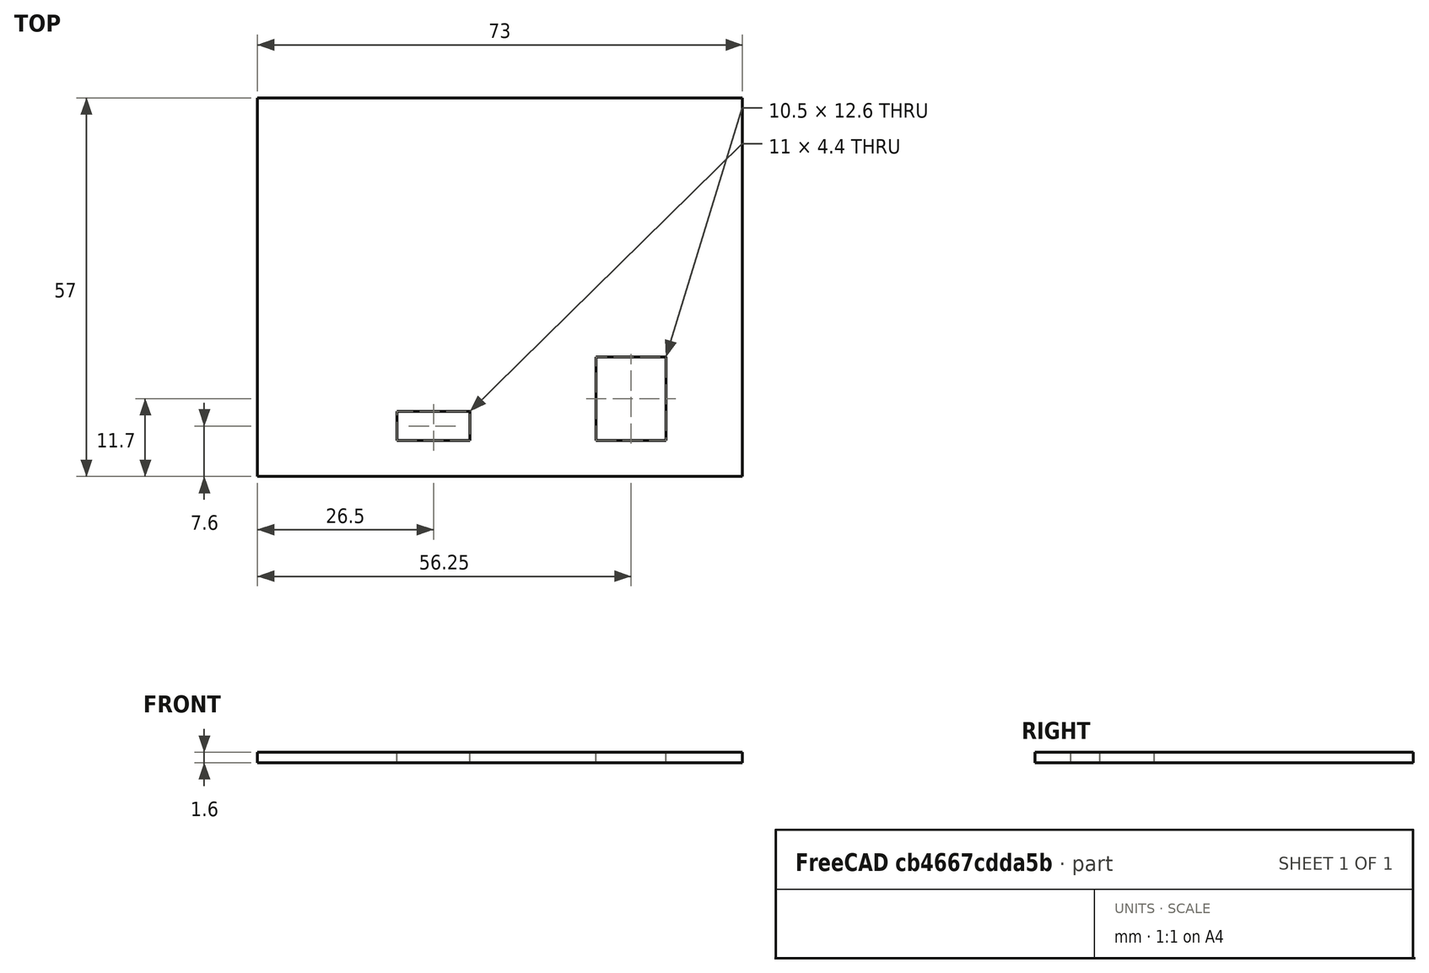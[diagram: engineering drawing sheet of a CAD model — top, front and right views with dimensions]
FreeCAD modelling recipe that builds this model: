
FCSTD DOCUMENT  (FreeCAD 0.18.4R)
Label: front
License: All rights reserved
LicenseURL: http://en.wikipedia.org/wiki/All_rights_reserved
objects: Mesh::Feature×1, Sketcher::SketchObject×1, PartDesign::Pad×1, PartDesign::Body×1
note: 4 computed .brp shape members not serialized (recipe doc carries the construction recipe); baked Part::Feature solids carry a one-line shape summary decoded from their .brp

FEATURE [Mesh::Feature] boxFront
FEATURE [Sketcher::SketchObject] Sketch
  MapMode = 5
  Support = -> [XY_Plane]
  sketch-geometry (12):
    g0: LineSegment StartX=0 StartY=0 StartZ=0 EndX=73 EndY=0 EndZ=0
    g1: LineSegment StartX=73 StartY=0 StartZ=0 EndX=73 EndY=57 EndZ=0
    g2: LineSegment StartX=73 StartY=57 StartZ=0 EndX=0 EndY=57 EndZ=0
    g3: LineSegment StartX=0 StartY=57 StartZ=0 EndX=0 EndY=0 EndZ=0
    g4: LineSegment StartX=51 StartY=18 StartZ=0 EndX=61.5 EndY=18 EndZ=0
    g5: LineSegment StartX=61.5 StartY=18 StartZ=0 EndX=61.5 EndY=5.4 EndZ=0
    g6: LineSegment StartX=61.5 StartY=5.4 StartZ=0 EndX=51 EndY=5.4 EndZ=0
    g7: LineSegment StartX=51 StartY=5.4 StartZ=0 EndX=51 EndY=18 EndZ=0
    g8: LineSegment StartX=21 StartY=9.8 StartZ=0 EndX=32 EndY=9.8 EndZ=0
    g9: LineSegment StartX=32 StartY=9.8 StartZ=0 EndX=32 EndY=5.4 EndZ=0
    g10: LineSegment StartX=32 StartY=5.4 StartZ=0 EndX=21 EndY=5.4 EndZ=0
    g11: LineSegment StartX=21 StartY=5.4 StartZ=0 EndX=21 EndY=9.8 EndZ=0
  constraints (35):
    c: Coincident(g0,g1)
    c: Coincident(g1,g2)
    c: Coincident(g2,g3)
    c: Coincident(g3,g0)
    c: Horizontal(g0)
    c: Horizontal(g2)
    c: Vertical(g1)
    c: Vertical(g3)
    c: Coincident(g0,g-1)
    c: Coincident(g4,g5)
    c: Coincident(g5,g6)
    c: Coincident(g6,g7)
    c: Coincident(g7,g4)
    c: Horizontal(g4)
    c: Horizontal(g6)
    c: Vertical(g5)
    c: Vertical(g7)
    c: Coincident(g8,g9)
    c: Coincident(g9,g10)
    c: Coincident(g10,g11)
    c: Coincident(g11,g8)
    c: Horizontal(g8)
    c: Horizontal(g10)
    c: Vertical(g9)
    c: Vertical(g11)
    c: DistanceX(g2,g2) = 73
    c: DistanceY(g3,g3) = 57
    c: DistanceX(g0,g10) = 21
    c: DistanceX(g0,g9) = 32
    c: DistanceY(g0,g10) = 5.4
    c: DistanceY(g0,g8) = 9.8
    c: DistanceX(g5,g0) = 11.5
    c: DistanceX(g6,g0) = 22
    c: DistanceY(g0,g5) = 5.4
    c: DistanceY(g0,g4) = 18
FEATURE [PartDesign::Pad] Pad
  Length = 1.6
  Length2 = 100
  Profile = -> Sketch
  Type = 0
FEATURE [PartDesign::Body] Body
  Group = -> [Sketch,Pad]
  Origin = -> Origin
  Tip = -> Pad
